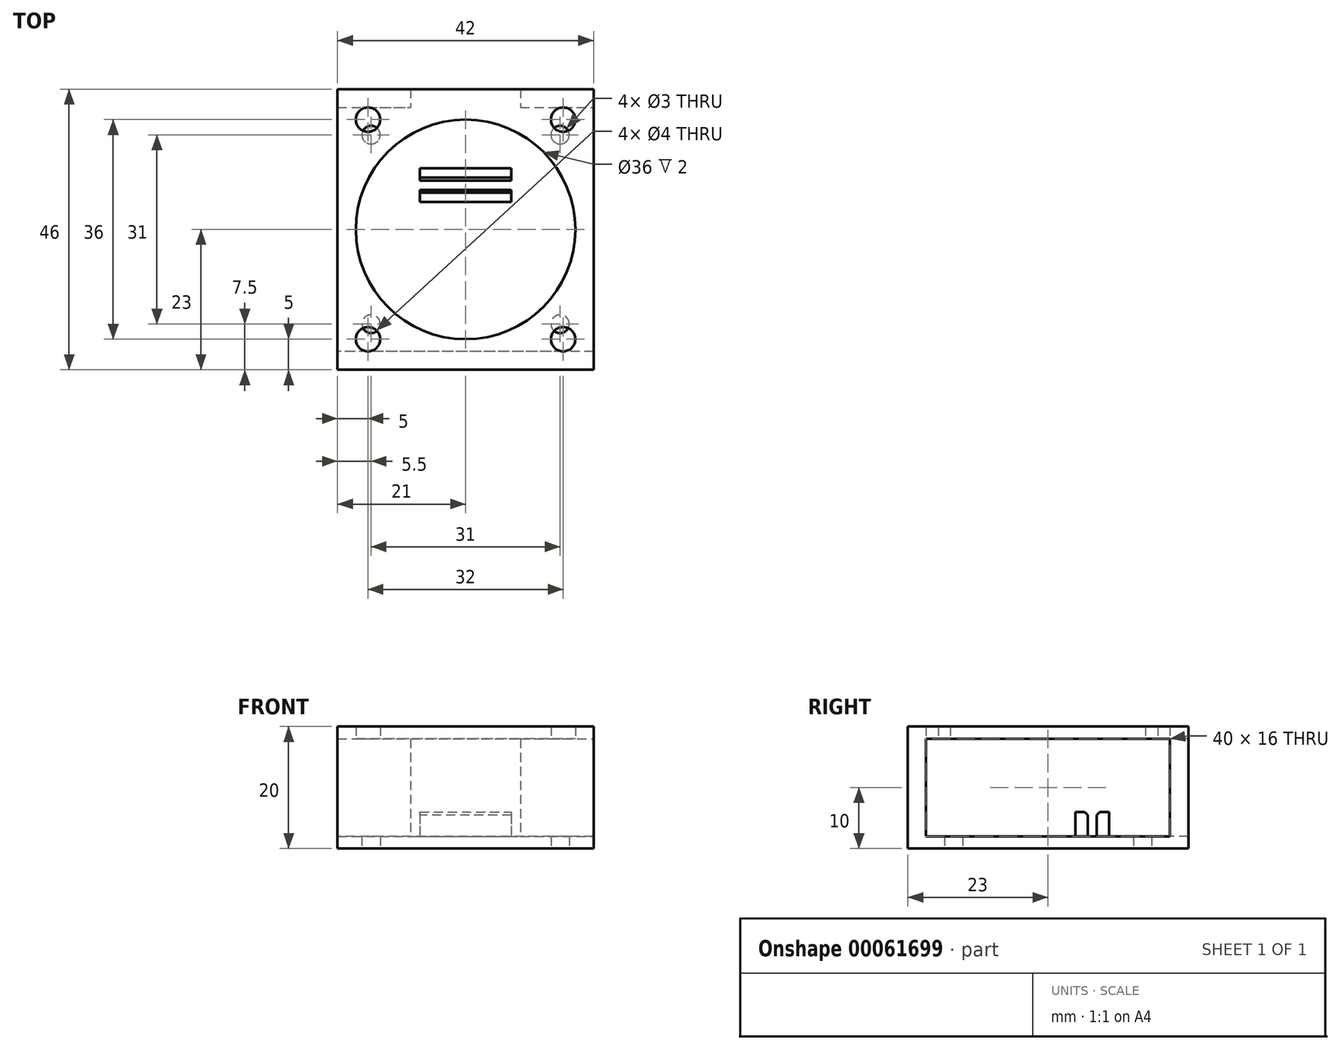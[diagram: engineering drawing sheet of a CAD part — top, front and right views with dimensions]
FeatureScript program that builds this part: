
annotation { "Feature Type Name" : "Feature", "Feature Type Description" : "" }
export const myFeature = defineFeature(function(context is Context, id is Id, definition is map)
    precondition{}
    {
        {
            var Q0;
            Q0=qCreatedBy(makeId("Top.planeOp"),FACE);
            var sketch = newSketch(context, id + "F0", { "sketchPlane" : qUnion([Q0])});
            skLineSegment(sketch, "E0.rect.bottom", {"start": v(21, 21) * mm, "end": v(-21, 21) * mm, "construction": true});
            skLineSegment(sketch, "E0.rect.top", {"start": v(21, -21) * mm, "end": v(-21, -21) * mm, "construction": true});
            skLineSegment(sketch, "E0.rect.left", {"start": v(21, 21) * mm, "end": v(21, -21) * mm, "construction": true});
            skLineSegment(sketch, "E0.rect.right", {"start": v(-21, 21) * mm, "end": v(-21, -21) * mm, "construction": true});
            skPoint(sketch, "E0.rect.middle", {"position": v(0, 0) * mm});
            skLineSegment(sketch, "E1.bottom", {"start": v(-21, 23) * mm, "end": v(21, 23) * mm});
            skLineSegment(sketch, "E1.top", {"start": v(-21, -23) * mm, "end": v(21, -23) * mm});
            skLineSegment(sketch, "E1.left", {"start": v(-21, 23) * mm, "end": v(-21, -23) * mm});
            skLineSegment(sketch, "E1.right", {"start": v(21, 23) * mm, "end": v(21, -23) * mm});
            skLineSegment(sketch, "E2", {"start": v(-21, 21) * mm, "end": v(-21, 21) * mm});
            skLineSegment(sketch, "E3", {"start": v(21, -21) * mm, "end": v(21, -21) * mm});
            skLineSegment(sketch, "E4.rect.bottom", {"start": v(-15.5, 15.5) * mm, "end": v(15.5, 15.5) * mm, "construction": true});
            skLineSegment(sketch, "E4.rect.top", {"start": v(-15.5, -15.5) * mm, "end": v(15.5, -15.5) * mm, "construction": true});
            skLineSegment(sketch, "E4.rect.left", {"start": v(-15.5, 15.5) * mm, "end": v(-15.5, -15.5) * mm, "construction": true});
            skLineSegment(sketch, "E4.rect.right", {"start": v(15.5, 15.5) * mm, "end": v(15.5, -15.5) * mm, "construction": true});
            skCircle(sketch, "E5", {"center": v(-15.5, 15.5) * mm, "radius": 1.5 * mm});
            skCircle(sketch, "E6", {"center": v(15.5, 15.5) * mm, "radius": 1.5 * mm});
            skCircle(sketch, "E7", {"center": v(15.5, -15.5) * mm, "radius": 1.5 * mm});
            skCircle(sketch, "E8", {"center": v(-15.5, -15.5) * mm, "radius": 1.5 * mm});
            skLineSegment(sketch, "E9", {"start": v(0, -21) * mm, "end": v(0, -23) * mm, "construction": true});
            skLineSegment(sketch, "E10", {"start": v(0, 21) * mm, "end": v(0, 23) * mm, "construction": true});
            skSolve(sketch);
        }
        {
            var Q0;
            Q0 = qSketchRegion(id + "F0", true);
            extrude(context, id + "F1", {"entities" : qUnion([Q0]), "depth" : 2 * mm});
        }
        {
            var Q0;
            Q0=makeQuery(id+"F1.opExtrude","CAP_FACE",FACE,{"disambiguationData":[OSD([sQuery(id+"F0.wireOp",EDGE,"E1.bottom"),sQuery(id+"F0.wireOp",EDGE,"E1.top"),sQuery(id+"F0.wireOp",EDGE,"E1.left"),sQuery(id+"F0.wireOp",EDGE,"E1.right"),sQuery(id+"F0.wireOp",EDGE,"E5"),sQuery(id+"F0.wireOp",EDGE,"E6"),sQuery(id+"F0.wireOp",EDGE,"E7"),sQuery(id+"F0.wireOp",EDGE,"E8")])],"isStart":false});
            var sketch = newSketch(context, id + "F2", { "sketchPlane" : qUnion([Q0])});
            skLineSegment(sketch, "E11.bottom", {"start": v(-21, 23) * mm, "end": v(-9, 23) * mm});
            skLineSegment(sketch, "E11.top", {"start": v(-21, 20) * mm, "end": v(-9, 20) * mm});
            skLineSegment(sketch, "E11.left", {"start": v(-21, 23) * mm, "end": v(-21, 20) * mm});
            skLineSegment(sketch, "E11.right", {"start": v(21, 23) * mm, "end": v(21, 20) * mm});
            skLineSegment(sketch, "E12.bottom", {"start": v(21, -23) * mm, "end": v(-21, -23) * mm});
            skLineSegment(sketch, "E12.top", {"start": v(21, -20) * mm, "end": v(-21, -20) * mm});
            skLineSegment(sketch, "E12.left", {"start": v(21, -23) * mm, "end": v(21, -20) * mm});
            skLineSegment(sketch, "E12.right", {"start": v(-21, -23) * mm, "end": v(-21, -20) * mm});
            skLineSegment(sketch, "E13.bottom", {"start": v(-9, 23) * mm, "end": v(9, 23) * mm});
            skLineSegment(sketch, "E13.left", {"start": v(-9, 23) * mm, "end": v(-9, 20) * mm});
            skLineSegment(sketch, "E13.right", {"start": v(9, 23) * mm, "end": v(9, 20) * mm});
            skLineSegment(sketch, "E14.trimOffspring", {"start": v(9, 23) * mm, "end": v(21, 23) * mm});
            skLineSegment(sketch, "E15.trimOffspring", {"start": v(9, 20) * mm, "end": v(21, 20) * mm});
            skSolve(sketch);
        }
        {
            var Q0;
            Q0 = qSketchRegion(id + "F2", true);
            extrude(context, id + "F3", {"entities" : qUnion([Q0]), "operationType" : NewBodyOperationType.ADD, "depth" : 16 * mm});
        }
        {
            var Q0;
            Q0=makeQuery(id+"F3.opExtrude","CAP_FACE",FACE,{"disambiguationData":[OSD([sQuery(id+"F2.wireOp",EDGE,"E12.bottom"),sQuery(id+"F2.wireOp",EDGE,"E12.top"),sQuery(id+"F2.wireOp",EDGE,"E12.left"),sQuery(id+"F2.wireOp",EDGE,"E12.right")])],"isStart":false});
            var sketch = newSketch(context, id + "F4", { "sketchPlane" : qUnion([Q0])});
            skLineSegment(sketch, "E16.bottom", {"start": v(-21, -23) * mm, "end": v(21, -23) * mm});
            skLineSegment(sketch, "E16.top", {"start": v(-21, 23) * mm, "end": v(21, 23) * mm});
            skLineSegment(sketch, "E16.left", {"start": v(-21, -23) * mm, "end": v(-21, 23) * mm});
            skLineSegment(sketch, "E16.right", {"start": v(21, -23) * mm, "end": v(21, 23) * mm});
            skCircle(sketch, "E17", {"center": v(0, 0) * mm, "radius": 18 * mm});
            skCircle(sketch, "E18", {"center": v(-16, 18) * mm, "radius": 2 * mm});
            skCircle(sketch, "E19", {"center": v(16, 18) * mm, "radius": 2 * mm});
            skCircle(sketch, "E20", {"center": v(16, -18) * mm, "radius": 2 * mm});
            skCircle(sketch, "E21", {"center": v(-16, -18) * mm, "radius": 2 * mm});
            skLineSegment(sketch, "E22", {"start": v(-16, 18) * mm, "end": v(-16, 23) * mm, "construction": true});
            skLineSegment(sketch, "E23", {"start": v(-16, 18) * mm, "end": v(-21, 18) * mm, "construction": true});
            skLineSegment(sketch, "E24", {"start": v(16, -18) * mm, "end": v(21, -18) * mm, "construction": true});
            skLineSegment(sketch, "E25", {"start": v(16, -18) * mm, "end": v(16, -23) * mm, "construction": true});
            skSolve(sketch);
        }
        {
            var Q0;
            Q0 = qSketchRegion(id + "F4", true);
            extrude(context, id + "F5", {"entities" : qUnion([Q0]), "operationType" : NewBodyOperationType.ADD, "depth" : 2 * mm});
        }
        {
            var Q0;
            Q0=makeQuery(id+"F1.opExtrude","CAP_FACE",FACE,{"disambiguationData":[OSD([sQuery(id+"F0.wireOp",EDGE,"E1.bottom"),sQuery(id+"F0.wireOp",EDGE,"E1.top"),sQuery(id+"F0.wireOp",EDGE,"E1.left"),sQuery(id+"F0.wireOp",EDGE,"E1.right"),sQuery(id+"F0.wireOp",EDGE,"E5"),sQuery(id+"F0.wireOp",EDGE,"E6"),sQuery(id+"F0.wireOp",EDGE,"E7"),sQuery(id+"F0.wireOp",EDGE,"E8")])],"isStart":false});
            var sketch = newSketch(context, id + "F6", { "sketchPlane" : qUnion([Q0])});
            skLineSegment(sketch, "E26.bottom", {"start": v(-7.5, 10) * mm, "end": v(7.5, 10) * mm});
            skLineSegment(sketch, "E26.top", {"start": v(-7.5, 8) * mm, "end": v(7.5, 8) * mm});
            skLineSegment(sketch, "E26.left", {"start": v(-7.5, 10) * mm, "end": v(-7.5, 8) * mm});
            skLineSegment(sketch, "E26.right", {"start": v(7.5, 10) * mm, "end": v(7.5, 8) * mm});
            skLineSegment(sketch, "E27", {"start": v(0, 0) * mm, "end": v(0, 10) * mm, "construction": true});
            skLineSegment(sketch, "E28.bottom", {"start": v(-7.5, 6.5) * mm, "end": v(7.5, 6.5) * mm});
            skLineSegment(sketch, "E28.top", {"start": v(-7.5, 4.5) * mm, "end": v(7.5, 4.5) * mm});
            skLineSegment(sketch, "E28.left", {"start": v(-7.5, 6.5) * mm, "end": v(-7.5, 4.5) * mm});
            skLineSegment(sketch, "E28.right", {"start": v(7.5, 6.5) * mm, "end": v(7.5, 4.5) * mm});
            skSolve(sketch);
        }
        {
            var Q0;
            Q0 = qSketchRegion(id + "F6", true);
            extrude(context, id + "F7", {"entities" : qUnion([Q0]), "operationType" : NewBodyOperationType.ADD, "depth" : 4 * mm});
        }
        {
            var Q0;
            Q0=makeQuery(id+"F7.opExtrude","CAP_EDGE",EDGE,{"disambiguationData":[OSD([sQuery(id+"F6.wireOp",EDGE,"E26.top")])],"isStart":false});
            var Q1;
            Q1=makeQuery(id+"F7.opExtrude","CAP_EDGE",EDGE,{"disambiguationData":[OSD([sQuery(id+"F6.wireOp",EDGE,"E28.bottom")])],"isStart":false});
            chamfer(context, id + "F8", {"entities" : qUnion([Q0, Q1]), "width" : 0.5 * mm, "tangentPropagation" : true});
        }
    });
